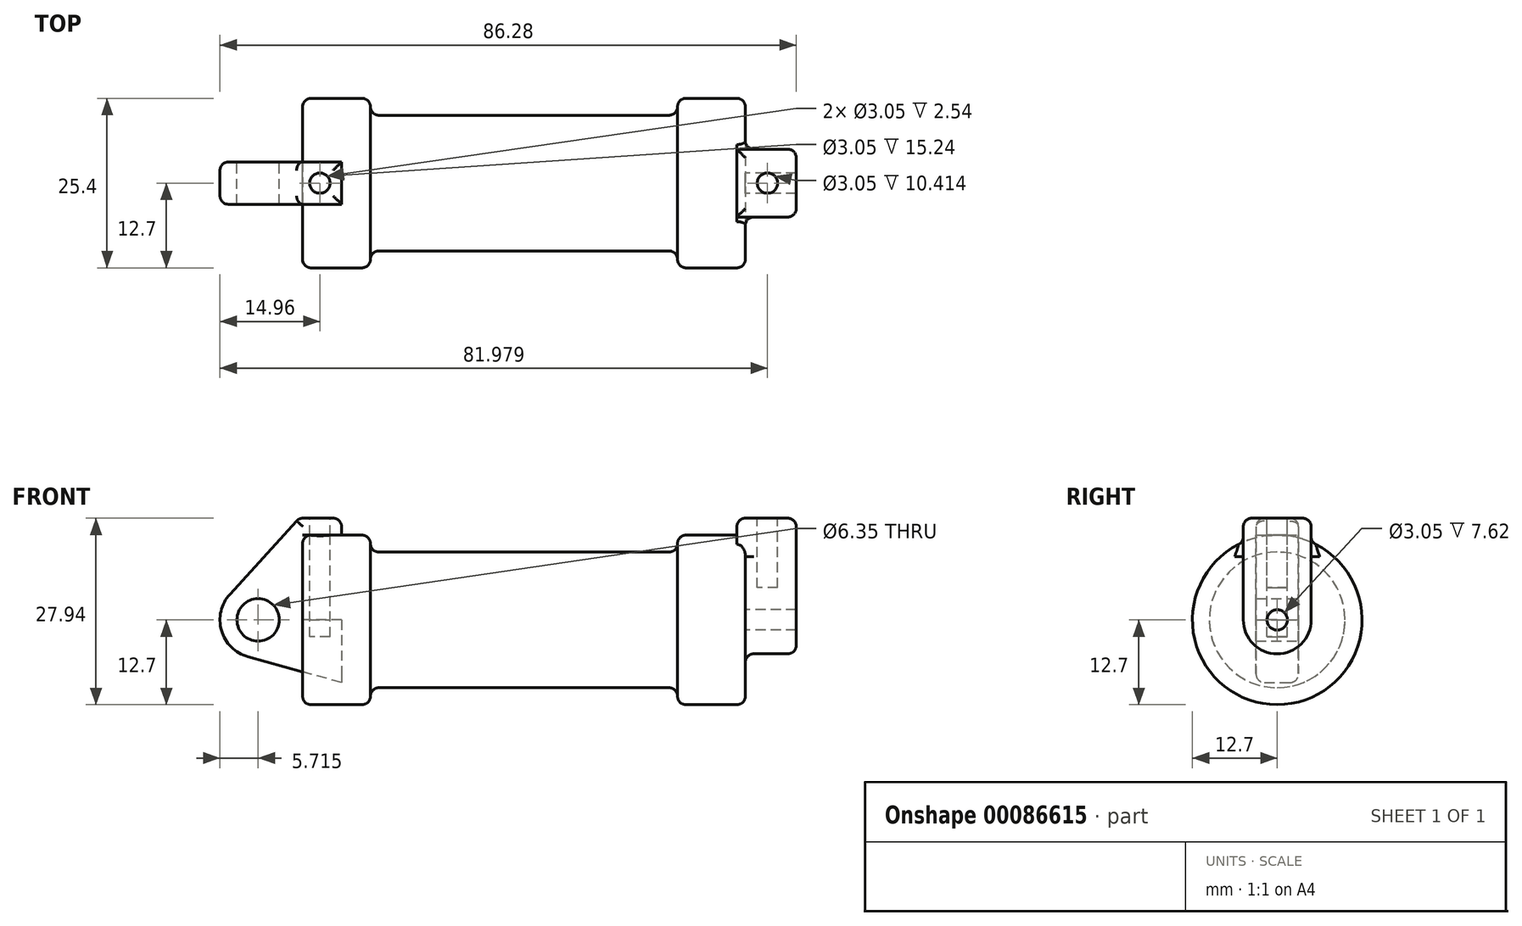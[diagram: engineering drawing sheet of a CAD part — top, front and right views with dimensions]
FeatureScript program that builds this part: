
annotation { "Feature Type Name" : "Feature", "Feature Type Description" : "" }
export const myFeature = defineFeature(function(context is Context, id is Id, definition is map)
    precondition{}
    {
        {
            var Q0;
            Q0=qCreatedBy(makeId("Front.planeOp"),FACE);
            var sketch = newSketch(context, id + "F0", { "sketchPlane" : qUnion([Q0])});
            skLineSegment(sketch, "E0", {"start": v(0, 0) * mm, "end": v(0, 12.7) * mm});
            skLineSegment(sketch, "E1", {"start": v(0, 12.7) * mm, "end": v(10.16, 12.7) * mm});
            skLineSegment(sketch, "E2", {"start": v(10.16, 12.7) * mm, "end": v(10.16, 10.16) * mm});
            skLineSegment(sketch, "E3", {"start": v(10.16, 10.16) * mm, "end": v(56.13, 10.16) * mm});
            skLineSegment(sketch, "E4", {"start": v(56.13, 10.16) * mm, "end": v(56.13, 12.7) * mm});
            skLineSegment(sketch, "E5", {"start": v(56.13, 12.7) * mm, "end": v(66.3, 12.7) * mm});
            skLineSegment(sketch, "E6", {"start": v(66.3, 12.7) * mm, "end": v(66.3, 0) * mm});
            skLineSegment(sketch, "E7", {"start": v(66.3, 0) * mm, "end": v(0, 0) * mm});
            skLineSegment(sketch, "E8", {"start": v(5.84, 15.24) * mm, "end": v(-0.5, 15.24) * mm});
            skLineSegment(sketch, "E9", {"start": v(-0.5, 15.24) * mm, "end": v(-10.88, 3.85) * mm});
            skLineSegment(sketch, "E10", {"start": v(0, 0) * mm, "end": v(-6.65, 0) * mm});
            skCircle(sketch, "E11", {"center": v(-6.65, 0) * mm, "radius": 5.72 * mm});
            skCircle(sketch, "E12", {"center": v(-6.65, 0) * mm, "radius": 3.18 * mm});
            skLineSegment(sketch, "E13", {"start": v(5.84, 15.24) * mm, "end": v(5.84, -9.4) * mm});
            skLineSegment(sketch, "E14", {"start": v(5.84, -9.4) * mm, "end": v(-8.18, -5.5) * mm});
            skSolve(sketch);
        }
        {
            var Q0;
            {var subQ0=sQuery(id+"F0.wireOp",EDGE,"E2");Q0=makeQuery(id+"F0.imprint","IMPRINT",FACE,{"disambiguationData":[TD([[makeQuery(id+"F0.imprint","IMPRINT",EDGE,{"derivedFrom":subQ0}),-1.0]])]});}
            var Q1;
            {var subQ0=sQuery(id+"F0.wireOp",EDGE,"E0");Q1=makeQuery(id+"F0.imprint","IMPRINT",FACE,{"disambiguationData":[TD([[makeQuery(id+"F0.imprint","IMPRINT",EDGE,{"derivedFrom":subQ0}),-1.0]])]});}
            var Q2;
            Q2=sQuery(id+"F0.wireOp",EDGE,"E7");
            revolve(context, id + "F1", {"entities" : qUnion([Q0, Q1]), "axis" : qUnion([Q2]), "revolveType" : RevolveType.FULL});
        }
        {
            var Q0;
            {var subQ4=sQuery(id+"F0.wireOp",EDGE,"E12");Q0=makeQuery(id+"F0.imprint","IMPRINT",FACE,{"disambiguationData":[TD([[makeQuery(id+"F0.imprint","IMPRINT",EDGE,{"derivedFrom":subQ4}),-1.0]])]});}
            var Q1;
            {var subQ3=sQuery(id+"F0.wireOp",EDGE,"E0");Q1=makeQuery(id+"F0.imprint","IMPRINT",FACE,{"disambiguationData":[TD([[makeQuery(id+"F0.imprint","IMPRINT",EDGE,{"derivedFrom":subQ3}),1.0]])]});}
            var Q2;
            {var subQ0=sQuery(id+"F0.wireOp",EDGE,"E14");Q2=makeQuery(id+"F0.imprint","IMPRINT",FACE,{"disambiguationData":[TD([[makeQuery(id+"F0.imprint","IMPRINT",EDGE,{"derivedFrom":subQ0}),-1.0]])]});}
            extrude(context, id + "F2", {"entities" : qUnion([Q0, Q1, Q2]), "endBound" : BoundingType.SYMMETRIC, "depth" : 6.35 * mm});
        }
        {
            var Q0;
            Q0=makeQuery(id+"F1.opRevolve","SWEPT_FACE",FACE,{"disambiguationData":[OSD([sQuery(id+"F0.wireOp",EDGE,"E6")])]});
            var sketch = newSketch(context, id + "F3", { "sketchPlane" : qUnion([Q0])});
            skCircle(sketch, "E15", {"center": v(0, 0) * mm, "radius": 1.52 * mm});
            skCircle(sketch, "E16", {"center": v(0, 0) * mm, "radius": 5.08 * mm});
            skLineSegment(sketch, "E17", {"start": v(-5.08, 0) * mm, "end": v(-5.08, 15.24) * mm});
            skLineSegment(sketch, "E18", {"start": v(5.08, 0) * mm, "end": v(5.08, 15.24) * mm});
            skLineSegment(sketch, "E19", {"start": v(-5.08, 15.24) * mm, "end": v(5.08, 15.24) * mm});
            skSolve(sketch);
        }
        {
            var Q0;
            {var subQ0=sQuery(id+"F3.wireOp",EDGE,"E17");var subQ1=sQuery(id+"F3.wireOp",EDGE,"E16");var subQ2=makeQuery(id+"F3.imprint","INTERSECT",VERTEX,{"derivedFrom":[subQ1,subQ0]});Q0=makeQuery(id+"F3.imprint","IMPRINT",FACE,{"disambiguationData":[TD([[makeQuery(id+"F3.imprint","IMPRINT",EDGE,{"disambiguationData":[TD([[subQ2,1.0]])],"derivedFrom":subQ1}),-1.0]])]});}
            var Q1;
            Q1=makeQuery(id+"F3.imprint","IMPRINT",FACE,{"disambiguationData":[TD([[makeQuery(id+"F3.imprint","IMPRINT",EDGE,{"derivedFrom":sQuery(id+"F3.wireOp",EDGE,"E15")}),-1.0]])]});
            var Q2;
            {var subQ0=sQuery(id+"F3.wireOp",EDGE,"E19");Q2=makeQuery(id+"F3.imprint","IMPRINT",FACE,{"disambiguationData":[TD([[makeQuery(id+"F3.imprint","IMPRINT",EDGE,{"derivedFrom":subQ0}),-1.0]])]});}
            extrude(context, id + "F4", {"entities" : qUnion([Q0, Q1, Q2]), "operationType" : NewBodyOperationType.ADD, "depth" : 7.62 * mm});
        }
        {
            var Q0;
            Q0=makeQuery(id+"F4.opExtrude","CAP_FACE",FACE,{"disambiguationData":[OSD([sQuery(id+"F3.wireOp",EDGE,"E15"),sQuery(id+"F3.wireOp",EDGE,"E16"),sQuery(id+"F3.wireOp",EDGE,"E17"),sQuery(id+"F3.wireOp",EDGE,"E18"),sQuery(id+"F3.wireOp",EDGE,"E19")])],"isStart":true});
            extrude(context, id + "F5", {"entities" : qUnion([Q0]), "operationType" : NewBodyOperationType.ADD, "depth" : 1.27 * mm});
        }
        {
            var Q0;
            {var subQ0=sQuery(id+"F3.wireOp",EDGE,"E19");Q0=makeQuery(id+"F5.boolean.opBoolean","MERGE",FACE,{"derivedFrom":[makeQuery(id+"F4.opExtrude","SWEPT_FACE",FACE,{"disambiguationData":[OSD([subQ0])]}),makeQuery(id+"F5.opExtrude","SWEPT_FACE",FACE,{"disambiguationData":[OSD([subQ0])]})]});}
            var sketch = newSketch(context, id + "F6", { "sketchPlane" : qUnion([Q0])});
            skCircle(sketch, "E20", {"center": v(69.6, 0) * mm, "radius": 1.52 * mm});
            skPoint(sketch, "E20.centerSnap0", {"position": v(65.02, 0) * mm});
            skSolve(sketch);
        }
        {
            var Q0;
            Q0=makeQuery(id+"F2.opExtrude","SWEPT_FACE",FACE,{"disambiguationData":[OSD([sQuery(id+"F0.wireOp",EDGE,"E8")])]});
            var sketch = newSketch(context, id + "F7", { "sketchPlane" : qUnion([Q0])});
            skCircle(sketch, "E21", {"center": v(2.59, 0) * mm, "radius": 1.52 * mm});
            skPoint(sketch, "E21.centerSnap0", {"position": v(-0.5, 0) * mm});
            skSolve(sketch);
        }
        {
            var Q0;
            Q0=makeQuery(id+"F7.imprint","IMPRINT",FACE,{"disambiguationData":[TD([[makeQuery(id+"F7.imprint","IMPRINT",EDGE,{"derivedFrom":sQuery(id+"F7.wireOp",EDGE,"E21")}),1.0]])]});
            extrude(context, id + "F8", {"entities" : qUnion([Q0]), "operationType" : NewBodyOperationType.REMOVE, "oppositeDirection" : true, "depth" : 17.78 * mm});
        }
        {
            var Q0;
            Q0=makeQuery(id+"F6.imprint","IMPRINT",FACE,{"disambiguationData":[TD([[makeQuery(id+"F6.imprint","IMPRINT",EDGE,{"derivedFrom":sQuery(id+"F6.wireOp",EDGE,"E20")}),1.0]])]});
            extrude(context, id + "F9", {"entities" : qUnion([Q0]), "operationType" : NewBodyOperationType.REMOVE, "oppositeDirection" : true, "depth" : 10.4 * mm});
        }
        {
            var Q0;
            Q0=makeQuery(id+"F2.opExtrude","CAP_EDGE",EDGE,{"disambiguationData":[OSD([sQuery(id+"F0.wireOp",EDGE,"E9")])],"isStart":true});
            fillet(context, id + "F10", {"entities" : qUnion([Q0]), "radius" : 1.27 * mm, "tangentPropagation" : true, "allowEdgeOverflow" : false});
        }
        {
            var Q0;
            Q0=makeQuery(id+"F1.opRevolve","SWEPT_EDGE",EDGE,{"disambiguationData":[OSD([sQuery(id+"F0.wireOp",EDGE,"E1"),sQuery(id+"F0.wireOp",EDGE,"E2")])]});
            var Q1;
            Q1=makeQuery(id+"F1.opRevolve","SWEPT_EDGE",EDGE,{"disambiguationData":[OSD([sQuery(id+"F0.wireOp",EDGE,"E0"),sQuery(id+"F0.wireOp",EDGE,"E1")])]});
            var Q2;
            Q2=makeQuery(id+"F2.opExtrude","CAP_EDGE",EDGE,{"disambiguationData":[OSD([sQuery(id+"F0.wireOp",EDGE,"E9")])],"isStart":false});
            fillet(context, id + "F11", {"entities" : qUnion([Q0, Q1, Q2]), "radius" : 1.27 * mm, "tangentPropagation" : true, "allowEdgeOverflow" : false});
        }
        {
            var Q0;
            Q0=makeQuery(id+"F2.opExtrude","CAP_EDGE",EDGE,{"disambiguationData":[OSD([sQuery(id+"F0.wireOp",EDGE,"E8")])],"isStart":true});
            var Q1;
            Q1=makeQuery(id+"F2.opExtrude","SWEPT_EDGE",EDGE,{"disambiguationData":[OSD([sQuery(id+"F0.wireOp",EDGE,"E8"),sQuery(id+"F0.wireOp",EDGE,"E9")])]});
            var Q2;
            Q2=makeQuery(id+"F2.opExtrude","CAP_EDGE",EDGE,{"disambiguationData":[OSD([sQuery(id+"F0.wireOp",EDGE,"E8")])],"isStart":false});
            var Q3;
            Q3=makeQuery(id+"F2.opExtrude","SWEPT_EDGE",EDGE,{"disambiguationData":[OSD([sQuery(id+"F0.wireOp",EDGE,"E8"),sQuery(id+"F0.wireOp",EDGE,"E13")])]});
            var Q4;
            Q4=makeQuery(id+"F1.opRevolve","SWEPT_EDGE",EDGE,{"disambiguationData":[OSD([sQuery(id+"F0.wireOp",EDGE,"E4"),sQuery(id+"F0.wireOp",EDGE,"E5")])]});
            var Q5;
            Q5=makeQuery(id+"F4.boolean.opBoolean","SPLIT",EDGE,{"disambiguationData":[OD(1.0)],"derivedFrom":makeQuery(id+"F1.opRevolve","SWEPT_EDGE",EDGE,{"disambiguationData":[OSD([sQuery(id+"F0.wireOp",EDGE,"E5"),sQuery(id+"F0.wireOp",EDGE,"E6")])]})});
            var Q6;
            Q6=makeQuery(id+"F5.opExtrude","CAP_EDGE",EDGE,{"disambiguationData":[OSD([sQuery(id+"F3.wireOp",EDGE,"E19")])],"isStart":false});
            var Q7;
            {var subQ0=sQuery(id+"F3.wireOp",EDGE,"E19");var subQ1=sQuery(id+"F3.wireOp",EDGE,"E17");Q7=makeQuery(id+"F5.boolean.opBoolean","MERGE",EDGE,{"derivedFrom":[makeQuery(id+"F4.opExtrude","SWEPT_EDGE",EDGE,{"disambiguationData":[OSD([subQ1,subQ0])]}),makeQuery(id+"F5.opExtrude","SWEPT_EDGE",EDGE,{"disambiguationData":[OSD([subQ1,subQ0])]})]});}
            var Q8;
            Q8=makeQuery(id+"F4.opExtrude","CAP_EDGE",EDGE,{"disambiguationData":[OSD([sQuery(id+"F3.wireOp",EDGE,"E19")])],"isStart":false});
            var Q9;
            {var subQ0=sQuery(id+"F3.wireOp",EDGE,"E19");var subQ1=sQuery(id+"F3.wireOp",EDGE,"E18");Q9=makeQuery(id+"F5.boolean.opBoolean","MERGE",EDGE,{"derivedFrom":[makeQuery(id+"F4.opExtrude","SWEPT_EDGE",EDGE,{"disambiguationData":[OSD([subQ1,subQ0])]}),makeQuery(id+"F5.opExtrude","SWEPT_EDGE",EDGE,{"disambiguationData":[OSD([subQ1,subQ0])]})]});}
            var Q10;
            Q10=makeQuery(id+"F4.opExtrude","CAP_EDGE",EDGE,{"disambiguationData":[OSD([sQuery(id+"F3.wireOp",EDGE,"E16")])],"isStart":false});
            var Q11;
            Q11=makeQuery(id+"F4.opExtrude","CAP_EDGE",EDGE,{"disambiguationData":[OSD([sQuery(id+"F3.wireOp",EDGE,"E18")])],"isStart":false});
            fillet(context, id + "F12", {"entities" : qUnion([Q0, Q1, Q2, Q3, Q4, Q5, Q6, Q7, Q8, Q9, Q10, Q11]), "radius" : 1.27 * mm, "tangentPropagation" : true, "allowEdgeOverflow" : false});
        }
        {
            var Q0;
            {var subQ0=sQuery(id+"F0.wireOp",EDGE,"E2");Q0=makeQuery(id+"F11.opFillet","BLEND_EDGE",EDGE,{"blendedFrom":[makeQuery(id+"F1.opRevolve","SWEPT_EDGE",EDGE,{"disambiguationData":[OSD([sQuery(id+"F0.wireOp",EDGE,"E1"),subQ0])]}),makeQuery(id+"F1.opRevolve","SWEPT_FACE",FACE,{"disambiguationData":[OSD([subQ0])]})],"blendedInto":[makeQuery(id+"F1.opRevolve","SWEPT_FACE",FACE,{"disambiguationData":[OSD([subQ0])]})]});}
            var Q1;
            {var subQ0=sQuery(id+"F0.wireOp",EDGE,"E4");Q1=makeQuery(id+"F12.opFillet","BLEND_EDGE",EDGE,{"blendedFrom":[makeQuery(id+"F1.opRevolve","SWEPT_EDGE",EDGE,{"disambiguationData":[OSD([subQ0,sQuery(id+"F0.wireOp",EDGE,"E5")])]}),makeQuery(id+"F1.opRevolve","SWEPT_FACE",FACE,{"disambiguationData":[OSD([subQ0])]})],"blendedInto":[makeQuery(id+"F1.opRevolve","SWEPT_FACE",FACE,{"disambiguationData":[OSD([subQ0])]})]});}
            var Q2;
            {var subQ3=sQuery(id+"F0.wireOp",EDGE,"E5");var subQ4=sQuery(id+"F0.wireOp",EDGE,"E6");Q2=makeQuery(id+"F12.opFillet","BLEND_EDGE",EDGE,{"blendedFrom":[makeQuery(id+"F4.boolean.opBoolean","SPLIT",EDGE,{"disambiguationData":[OD(1.0)],"derivedFrom":makeQuery(id+"F1.opRevolve","SWEPT_EDGE",EDGE,{"disambiguationData":[OSD([subQ3,subQ4])]})}),makeQuery(id+"F4.boolean.opBoolean","SPLIT",FACE,{"disambiguationData":[TD([makeQuery(id+"F1.opRevolve","SWEPT_FACE",FACE,{"disambiguationData":[OSD([subQ3])]})])],"derivedFrom":makeQuery(id+"F1.opRevolve","SWEPT_FACE",FACE,{"disambiguationData":[OSD([subQ4])]})})],"blendedInto":[makeQuery(id+"F4.boolean.opBoolean","SPLIT",FACE,{"disambiguationData":[TD([makeQuery(id+"F1.opRevolve","SWEPT_FACE",FACE,{"disambiguationData":[OSD([subQ3])]})])],"derivedFrom":makeQuery(id+"F1.opRevolve","SWEPT_FACE",FACE,{"disambiguationData":[OSD([subQ4])]})})]});}
            var Q3;
            {var subQ0=sQuery(id+"F3.wireOp",EDGE,"E16");var subQ1=sQuery(id+"F3.wireOp",EDGE,"E17");Q3=makeQuery(id+"F4.boolean.opBoolean","SPLIT",EDGE,{"disambiguationData":[TD([makeQuery(id+"F4.opExtrude","SWEPT_FACE",FACE,{"disambiguationData":[OSD([subQ0])]})])],"derivedFrom":makeQuery(id+"F4.opExtrude","CAP_EDGE",EDGE,{"disambiguationData":[OSD([subQ1])],"isStart":true})});}
            var Q4;
            Q4=makeQuery(id+"F1.opRevolve","SWEPT_EDGE",EDGE,{"disambiguationData":[OSD([sQuery(id+"F0.wireOp",EDGE,"E2"),sQuery(id+"F0.wireOp",EDGE,"E3")])]});
            var Q5;
            Q5=makeQuery(id+"F1.opRevolve","SWEPT_EDGE",EDGE,{"disambiguationData":[OSD([sQuery(id+"F0.wireOp",EDGE,"E3"),sQuery(id+"F0.wireOp",EDGE,"E4")])]});
            fillet(context, id + "F13", {"entities" : qUnion([Q0, Q1, Q2, Q3, Q4, Q5]), "radius" : 1.27 * mm, "tangentPropagation" : true, "allowEdgeOverflow" : false});
        }
    });
